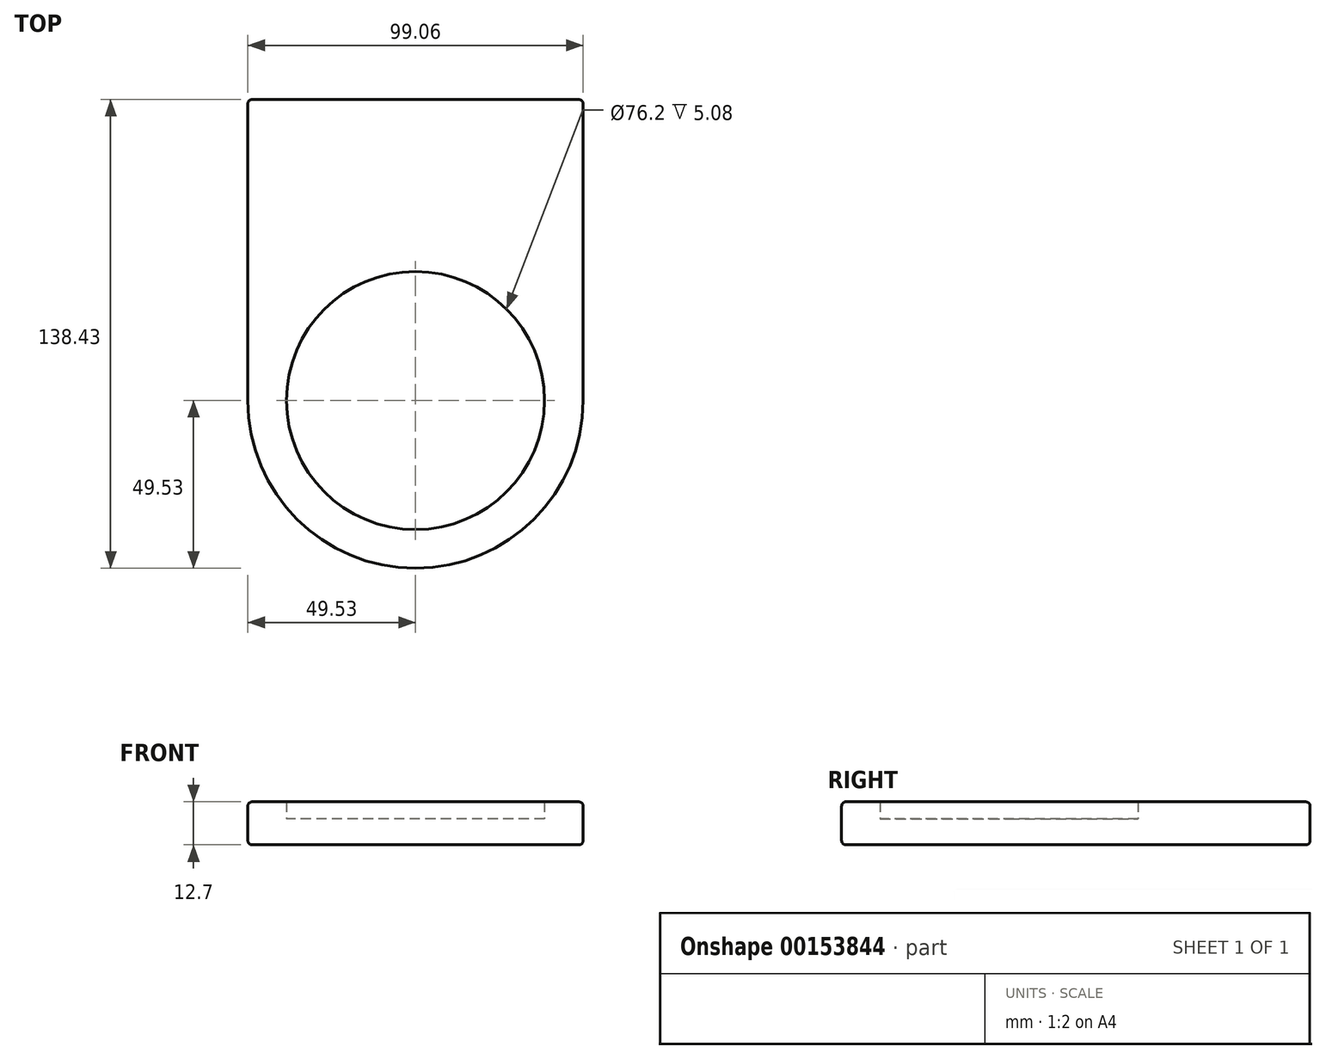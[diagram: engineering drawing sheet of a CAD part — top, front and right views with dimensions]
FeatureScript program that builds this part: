
annotation { "Feature Type Name" : "Feature", "Feature Type Description" : "" }
export const myFeature = defineFeature(function(context is Context, id is Id, definition is map)
    precondition{}
    {
        {
            var Q0;
            Q0=qCreatedBy(makeId("Top.planeOp"),FACE);
            var sketch = newSketch(context, id + "F0", { "sketchPlane" : qUnion([Q0])});
            skArc(sketch, "E0", {"start": v(-49.53, 0) * mm, "mid": v(0, -49.53) * mm, "end": v(49.53, 0) * mm});
            skLineSegment(sketch, "E1", {"start": v(-49.53, 0) * mm, "end": v(-49.53, 88.9) * mm});
            skLineSegment(sketch, "E2", {"start": v(49.53, 0) * mm, "end": v(49.53, 88.9) * mm});
            skLineSegment(sketch, "E3", {"start": v(-49.53, 88.9) * mm, "end": v(49.53, 88.9) * mm});
            skCircle(sketch, "E4", {"center": v(0, 0) * mm, "radius": 38.1 * mm});
            skLineSegment(sketch, "E5", {"start": v(0, 88.9) * mm, "end": v(0, -49.53) * mm});
            skSolve(sketch);
        }
        {
            var Q0;
            Q0=makeQuery(id+"F0.imprint","IMPRINT",FACE,{"disambiguationData":[TD([[makeQuery(id+"F0.imprint","IMPRINT",EDGE,{"derivedFrom":sQuery(id+"F0.wireOp",EDGE,"E0")}),1.0]])]});
            extrude(context, id + "F1", {"entities" : qUnion([Q0]), "depth" : 12.7 * mm});
        }
        {
            var Q0;
            Q0=makeQuery(id+"F0.imprint","IMPRINT",FACE,{"disambiguationData":[TD([[makeQuery(id+"F0.imprint","IMPRINT",EDGE,{"derivedFrom":sQuery(id+"F0.wireOp",EDGE,"E4")}),1.0]])]});
            extrude(context, id + "F2", {"entities" : qUnion([Q0]), "operationType" : NewBodyOperationType.ADD, "depth" : 7.62 * mm});
        }
        {
            var Q0;
            Q0=makeQuery(id+"F1.opExtrude","CAP_EDGE",EDGE,{"disambiguationData":[OSD([sQuery(id+"F0.wireOp",EDGE,"E2")])],"isStart":false});
            var Q1;
            Q1=makeQuery(id+"F1.opExtrude","SWEPT_EDGE",EDGE,{"disambiguationData":[OSD([sQuery(id+"F0.wireOp",EDGE,"E2"),sQuery(id+"F0.wireOp",EDGE,"E3")])]});
            var Q2;
            Q2=makeQuery(id+"F1.opExtrude","CAP_EDGE",EDGE,{"disambiguationData":[OSD([sQuery(id+"F0.wireOp",EDGE,"E3")])],"isStart":false});
            var Q3;
            Q3=makeQuery(id+"F1.opExtrude","CAP_EDGE",EDGE,{"disambiguationData":[OSD([sQuery(id+"F0.wireOp",EDGE,"E3")])],"isStart":true});
            var Q4;
            Q4=makeQuery(id+"F1.opExtrude","CAP_EDGE",EDGE,{"disambiguationData":[OSD([sQuery(id+"F0.wireOp",EDGE,"E2")])],"isStart":true});
            var Q5;
            Q5=makeQuery(id+"F1.opExtrude","SWEPT_EDGE",EDGE,{"disambiguationData":[OSD([sQuery(id+"F0.wireOp",EDGE,"E1"),sQuery(id+"F0.wireOp",EDGE,"E3")])]});
            fillet(context, id + "F3", {"entities" : qUnion([Q0, Q1, Q2, Q3, Q4, Q5]), "radius" : 1.27 * mm, "tangentPropagation" : true, "allowEdgeOverflow" : false});
        }
    });
